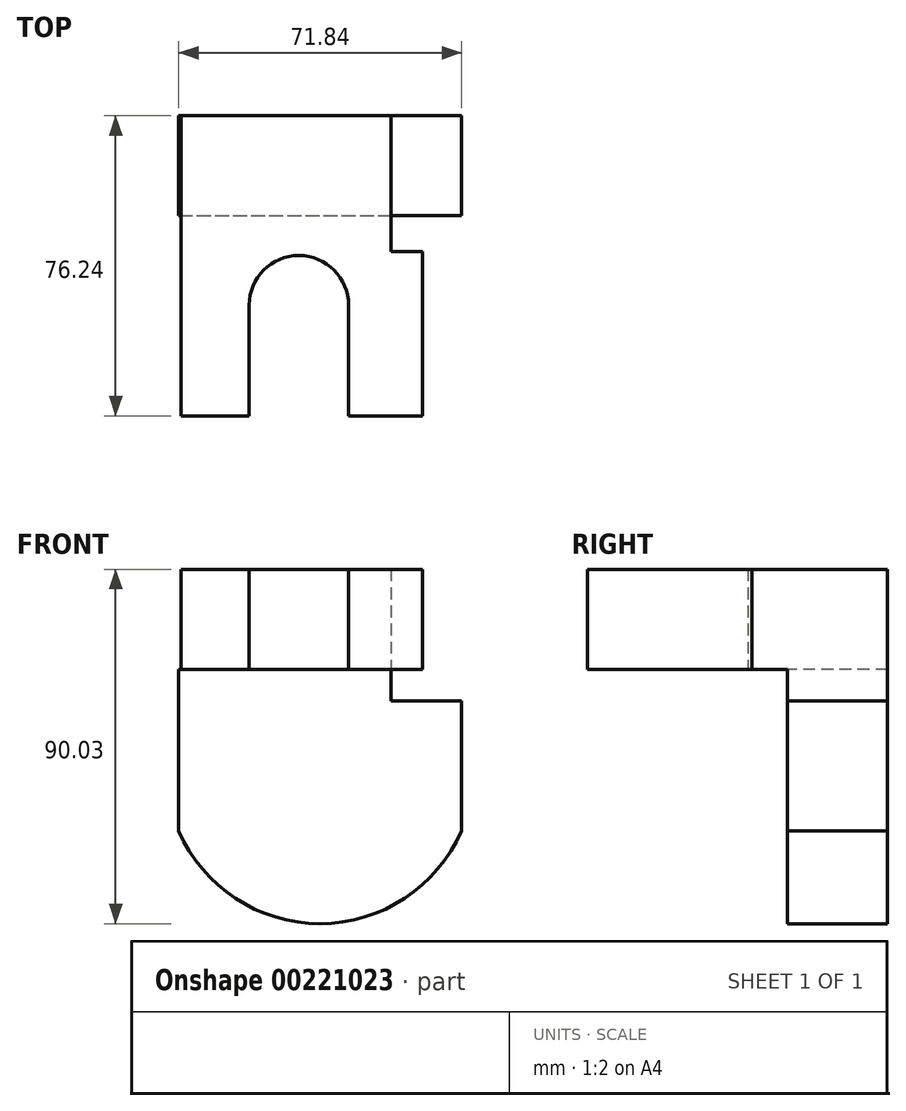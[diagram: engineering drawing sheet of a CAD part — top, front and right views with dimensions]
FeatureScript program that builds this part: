
annotation { "Feature Type Name" : "Feature", "Feature Type Description" : "" }
export const myFeature = defineFeature(function(context is Context, id is Id, definition is map)
    precondition{}
    {
        {
            var Q0;
            Q0=qCreatedBy(makeId("Front.planeOp"),FACE);
            var sketch = newSketch(context, id + "F0", { "sketchPlane" : qUnion([Q0])});
            skLineSegment(sketch, "E0", {"start": v(-53.95, 0) * mm, "end": v(-53.95, -41.03) * mm});
            skLineSegment(sketch, "E1", {"start": v(-53.95, -41.03) * mm, "end": v(-53.95, 0) * mm});
            skLineSegment(sketch, "E2", {"start": v(-53.95, 0) * mm, "end": v(0, 0) * mm});
            skLineSegment(sketch, "E3", {"start": v(0, 0) * mm, "end": v(0, -8.1) * mm});
            skLineSegment(sketch, "E4", {"start": v(0, -8.1) * mm, "end": v(17.89, -8.1) * mm});
            skLineSegment(sketch, "E5", {"start": v(17.89, -8.1) * mm, "end": v(17.89, -41.03) * mm});
            skArc(sketch, "E6", {"start": v(-53.95, -41.03) * mm, "mid": v(-18.03, -64.63) * mm, "end": v(17.89, -41.03) * mm});
            skSolve(sketch);
        }
        {
            var Q0;
            Q0 = qSketchRegion(id + "F0", true);
            extrude(context, id + "F1", {"entities" : qUnion([Q0]), "depth" : 25.4 * mm});
        }
        {
            var Q0;
            Q0=qCreatedBy(makeId("Top.planeOp"),FACE);
            var sketch = newSketch(context, id + "F2", { "sketchPlane" : qUnion([Q0])});
            skLineSegment(sketch, "E7", {"start": v(0, -25.7) * mm, "end": v(0, -34.5) * mm});
            skLineSegment(sketch, "E8", {"start": v(0, -34.5) * mm, "end": v(7.95, -34.5) * mm});
            skLineSegment(sketch, "E9", {"start": v(7.95, -34.5) * mm, "end": v(7.95, -76.24) * mm});
            skLineSegment(sketch, "E10", {"start": v(7.95, -76.24) * mm, "end": v(-10.79, -76.24) * mm});
            skLineSegment(sketch, "E11", {"start": v(-10.79, -76.24) * mm, "end": v(-10.79, -48.13) * mm});
            skLineSegment(sketch, "E12", {"start": v(-53.38, -25.98) * mm, "end": v(-53.38, -76.24) * mm});
            skLineSegment(sketch, "E13", {"start": v(-53.38, -76.24) * mm, "end": v(-36.06, -76.24) * mm});
            skLineSegment(sketch, "E14", {"start": v(-36.06, -76.24) * mm, "end": v(-36.06, -48.13) * mm});
            skLineSegment(sketch, "E15", {"start": v(0, -25.7) * mm, "end": v(0, 0) * mm});
            skLineSegment(sketch, "E16", {"start": v(0, 0) * mm, "end": v(-53.38, 0) * mm});
            skLineSegment(sketch, "E17", {"start": v(-53.38, 0) * mm, "end": v(-53.38, -25.98) * mm});
            skArc(sketch, "E18", {"start": v(-10.79, -48.13) * mm, "mid": v(-23.42, -35.5) * mm, "end": v(-36.06, -48.13) * mm});
            skSolve(sketch);
        }
        {
            var Q0;
            Q0 = qSketchRegion(id + "F2", true);
            extrude(context, id + "F3", {"entities" : qUnion([Q0]), "operationType" : NewBodyOperationType.ADD, "depth" : 25.4 * mm});
        }
    });
